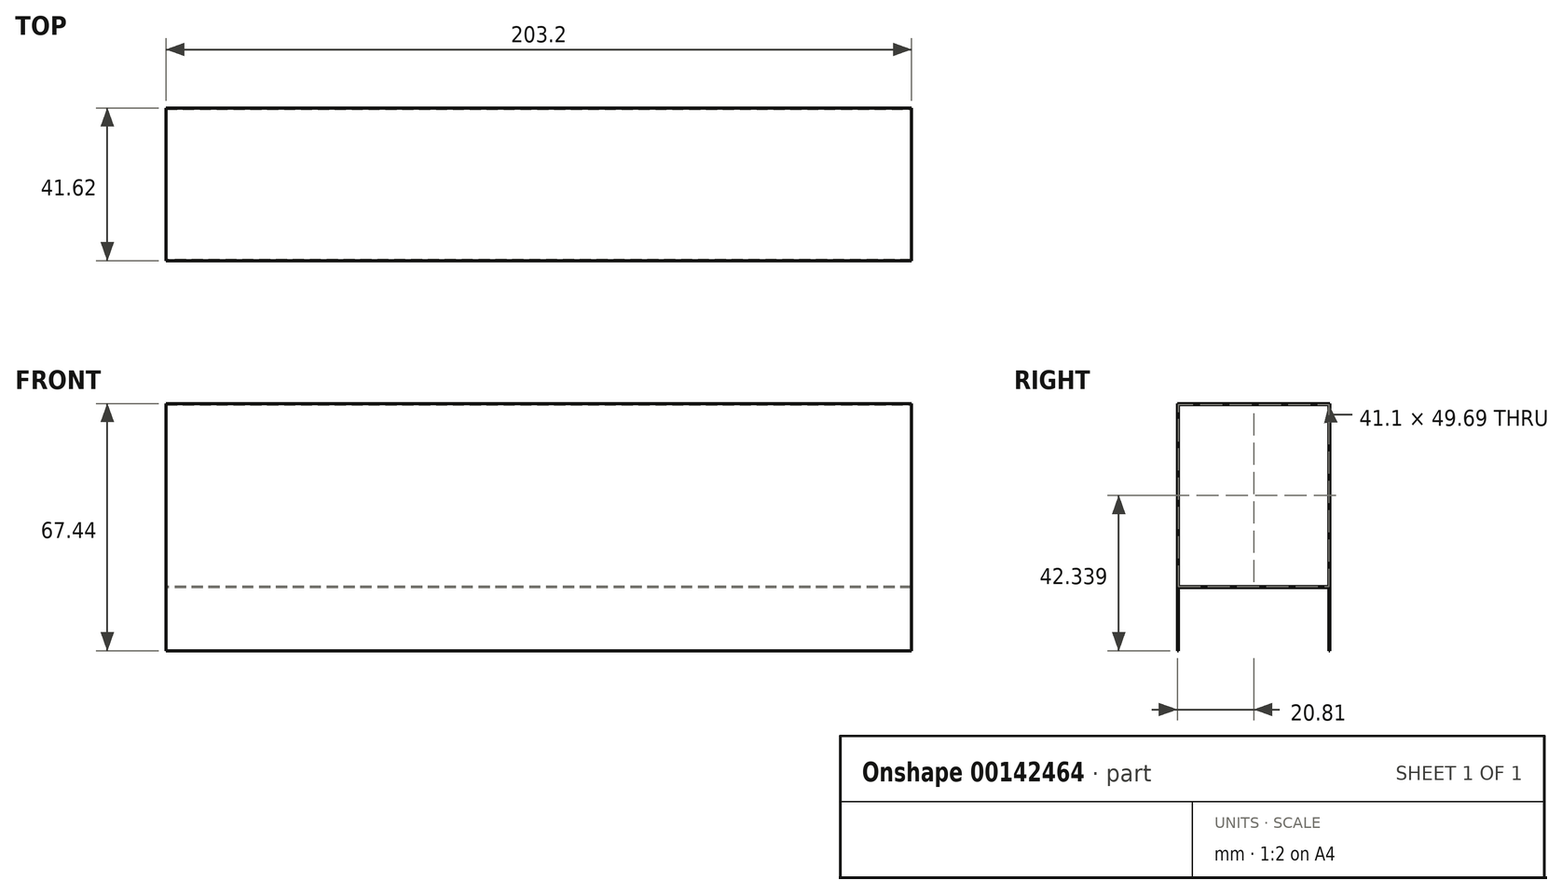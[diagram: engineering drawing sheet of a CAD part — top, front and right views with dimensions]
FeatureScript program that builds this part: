
annotation { "Feature Type Name" : "Feature", "Feature Type Description" : "" }
export const myFeature = defineFeature(function(context is Context, id is Id, definition is map)
    precondition{}
    {
        {
            var Q0;
            Q0=qCreatedBy(makeId("Right.planeOp"),FACE);
            var sketch = newSketch(context, id + "F0", { "sketchPlane" : qUnion([Q0])});
            skLineSegment(sketch, "E0.bottom", {"start": v(-20.55, -33.72) * mm, "end": v(-20.8, -33.72) * mm});
            skLineSegment(sketch, "E0.top", {"start": v(20.8, 33.72) * mm, "end": v(-20.8, 33.72) * mm});
            skLineSegment(sketch, "E0.left", {"start": v(20.8, -33.72) * mm, "end": v(20.8, 33.72) * mm});
            skLineSegment(sketch, "E0.right", {"start": v(-20.8, -33.72) * mm, "end": v(-20.8, 33.72) * mm});
            skPoint(sketch, "E0.middle", {"position": v(0, 0) * mm});
            skLineSegment(sketch, "E1.0", {"start": v(-20.55, -16.23) * mm, "end": v(-20.55, 33.46) * mm});
            skLineSegment(sketch, "E2", {"start": v(-20.55, -16.48) * mm, "end": v(20.55, -16.48) * mm});
            skLineSegment(sketch, "E3.0", {"start": v(20.55, 33.46) * mm, "end": v(-20.55, 33.46) * mm});
            skLineSegment(sketch, "E4.0", {"start": v(20.55, -16.23) * mm, "end": v(20.55, 33.46) * mm});
            skLineSegment(sketch, "E5.0", {"start": v(-20.55, -16.23) * mm, "end": v(20.55, -16.23) * mm});
            skLineSegment(sketch, "E6", {"start": v(20.55, -33.72) * mm, "end": v(20.8, -33.72) * mm});
            skLineSegment(sketch, "E7", {"start": v(-20.55, -16.48) * mm, "end": v(-20.55, -33.72) * mm});
            skLineSegment(sketch, "E8", {"start": v(20.55, -16.48) * mm, "end": v(20.55, -33.72) * mm});
            skSolve(sketch);
        }
        {
            var Q0;
            Q0 = qSketchRegion(id + "F0", true);
            extrude(context, id + "F1", {"entities" : qUnion([Q0]), "endBound" : BoundingType.SYMMETRIC, "depth" : 203.2 * mm});
        }
    });
